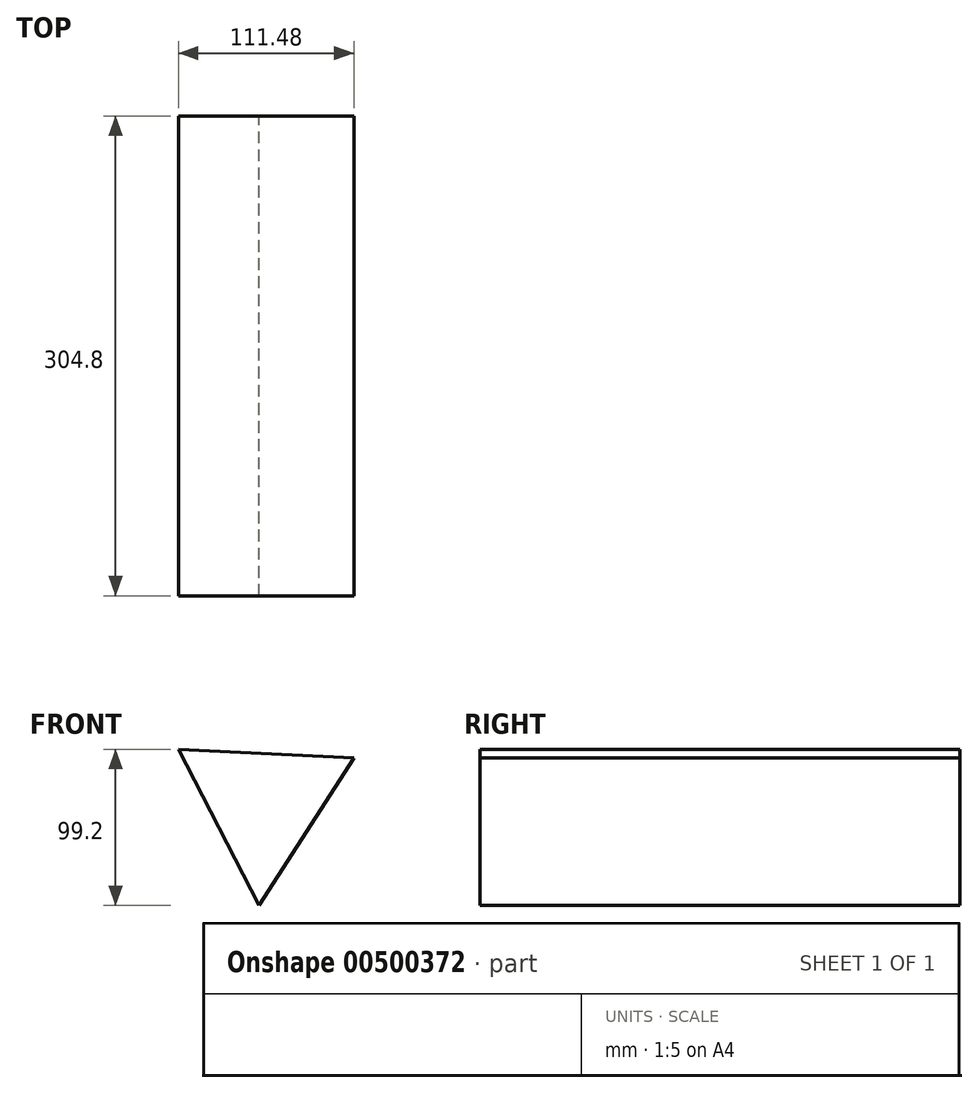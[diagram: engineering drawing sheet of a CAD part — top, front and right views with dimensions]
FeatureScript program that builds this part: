
annotation { "Feature Type Name" : "Feature", "Feature Type Description" : "" }
export const myFeature = defineFeature(function(context is Context, id is Id, definition is map)
    precondition{}
    {
        {
            var Q0;
            Q0=qCreatedBy(makeId("Front.planeOp"),FACE);
            var sketch = newSketch(context, id + "F0", { "sketchPlane" : qUnion([Q0])});
            skCircle(sketch, "E0.cCircle", {"center": v(0, 0) * mm, "radius": 64.44 * mm, "construction": true});
            skLineSegment(sketch, "E0.0", {"start": v(-54.21, 34.83) * mm, "end": v(57.27, 29.54) * mm});
            skLineSegment(sketch, "E0.1", {"start": v(57.27, 29.54) * mm, "end": v(-3.06, -64.37) * mm});
            skLineSegment(sketch, "E0.2", {"start": v(-3.06, -64.37) * mm, "end": v(-54.21, 34.83) * mm});
            skSolve(sketch);
        }
        {
            var Q0;
            Q0=makeQuery(id+"F0.imprint","IMPRINT",FACE,{"disambiguationData":[TD([[makeQuery(id+"F0.imprint","IMPRINT",EDGE,{"derivedFrom":sQuery(id+"F0.wireOp",EDGE,"E0.0")}),-1.0]])]});
            extrude(context, id + "F1", {"entities" : qUnion([Q0]), "depth" : 304.8 * mm});
        }
    });
